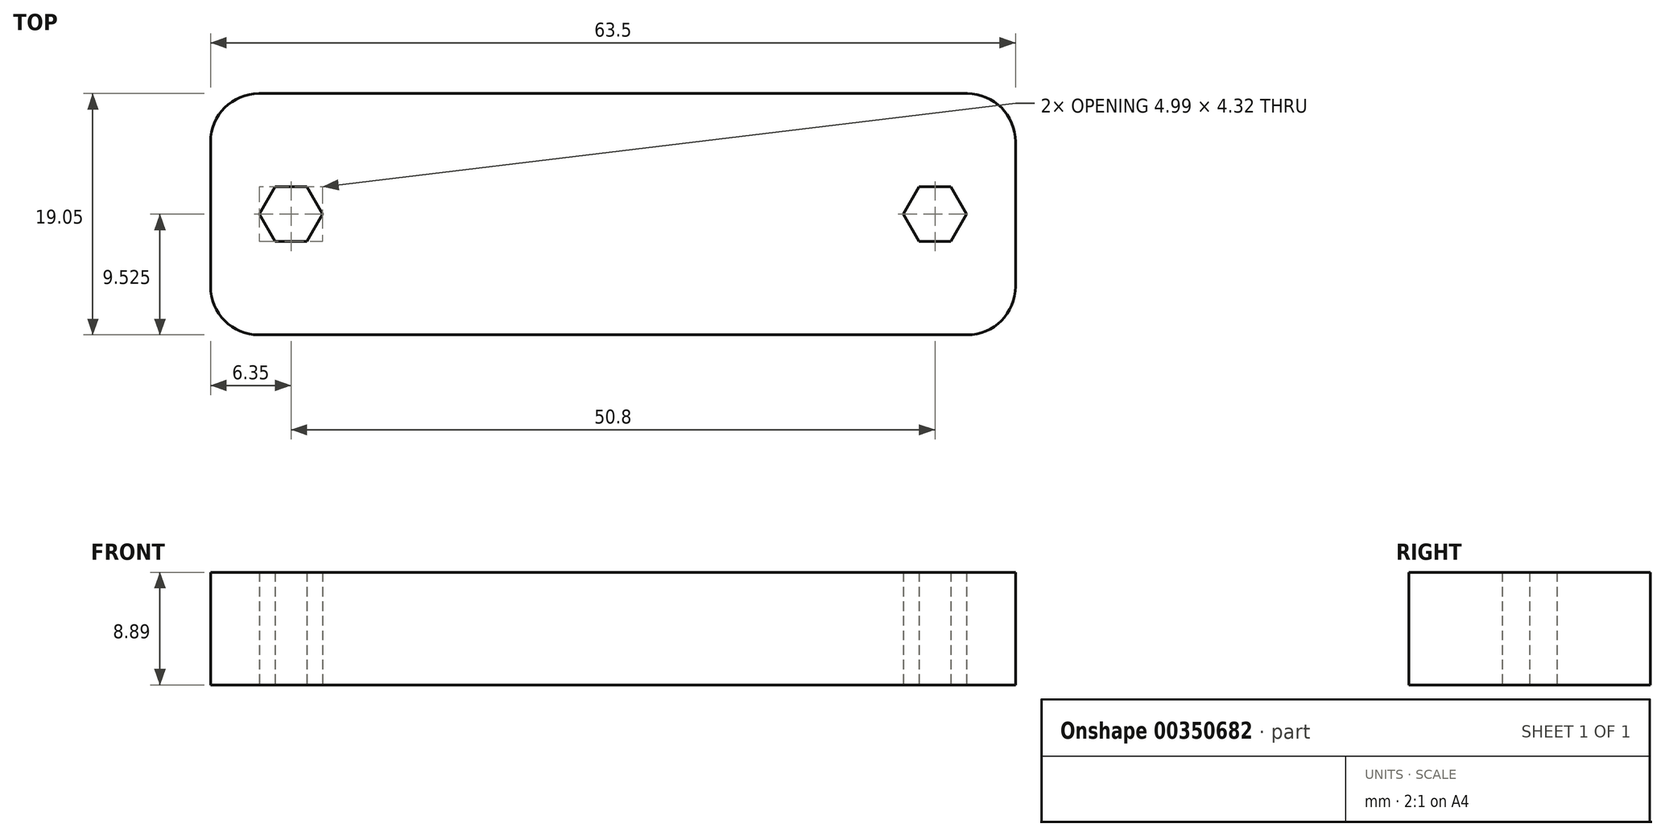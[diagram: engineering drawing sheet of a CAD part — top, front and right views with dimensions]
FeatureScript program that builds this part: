
annotation { "Feature Type Name" : "Feature", "Feature Type Description" : "" }
export const myFeature = defineFeature(function(context is Context, id is Id, definition is map)
    precondition{}
    {
        {
            var Q0;
            Q0=qCreatedBy(makeId("Top.planeOp"),FACE);
            var sketch = newSketch(context, id + "F0", { "sketchPlane" : qUnion([Q0])});
            skLineSegment(sketch, "E0.bottom", {"start": v(0, 0) * mm, "end": v(63.5, 0) * mm});
            skLineSegment(sketch, "E0.top", {"start": v(0, 19.05) * mm, "end": v(63.5, 19.05) * mm});
            skLineSegment(sketch, "E0.left", {"start": v(0, 0) * mm, "end": v(0, 19.05) * mm});
            skLineSegment(sketch, "E0.right", {"start": v(63.5, 0) * mm, "end": v(63.5, 19.05) * mm});
            skCircle(sketch, "E1.cCircle", {"center": v(6.35, 9.53) * mm, "radius": 2.16 * mm, "construction": true});
            skLineSegment(sketch, "E1.0", {"start": v(5.1, 11.68) * mm, "end": v(7.6, 11.68) * mm});
            skLineSegment(sketch, "E1.1", {"start": v(7.6, 11.68) * mm, "end": v(8.84, 9.53) * mm});
            skLineSegment(sketch, "E1.2", {"start": v(8.84, 9.52) * mm, "end": v(7.6, 7.37) * mm});
            skLineSegment(sketch, "E1.3", {"start": v(7.6, 7.37) * mm, "end": v(5.1, 7.37) * mm});
            skLineSegment(sketch, "E1.4", {"start": v(5.1, 7.37) * mm, "end": v(3.86, 9.53) * mm});
            skLineSegment(sketch, "E1.5", {"start": v(3.86, 9.53) * mm, "end": v(5.1, 11.68) * mm});
            skPoint(sketch, "E1.0.midPoint", {"position": v(6.35, 11.68) * mm});
            skCircle(sketch, "E2.cCircle", {"center": v(57.15, 9.53) * mm, "radius": 2.16 * mm, "construction": true});
            skLineSegment(sketch, "E2.0", {"start": v(55.9, 11.68) * mm, "end": v(58.4, 11.68) * mm});
            skLineSegment(sketch, "E2.1", {"start": v(58.4, 11.68) * mm, "end": v(59.64, 9.53) * mm});
            skLineSegment(sketch, "E2.2", {"start": v(59.64, 9.52) * mm, "end": v(58.4, 7.37) * mm});
            skLineSegment(sketch, "E2.3", {"start": v(58.4, 7.37) * mm, "end": v(55.9, 7.37) * mm});
            skLineSegment(sketch, "E2.4", {"start": v(55.9, 7.37) * mm, "end": v(54.66, 9.53) * mm});
            skLineSegment(sketch, "E2.5", {"start": v(54.66, 9.53) * mm, "end": v(55.9, 11.68) * mm});
            skPoint(sketch, "E2.0.midPoint", {"position": v(57.15, 11.68) * mm});
            skLineSegment(sketch, "E3", {"start": v(31.75, 19.05) * mm, "end": v(31.75, 0) * mm, "construction": true});
            skSolve(sketch);
        }
        {
            var Q0;
            Q0=makeQuery(id+"F0.imprint","IMPRINT",FACE,{"disambiguationData":[TD([[makeQuery(id+"F0.imprint","IMPRINT",EDGE,{"derivedFrom":sQuery(id+"F0.wireOp",EDGE,"E0.bottom")}),1.0]])]});
            extrude(context, id + "F1", {"entities" : qUnion([Q0]), "depth" : 8.9 * mm});
        }
        {
            var Q0;
            Q0=makeQuery(id+"F1.opExtrude","SWEPT_EDGE",EDGE,{"disambiguationData":[OSD([sQuery(id+"F0.wireOp",EDGE,"E0.bottom"),sQuery(id+"F0.wireOp",EDGE,"E0.left")])]});
            var Q1;
            Q1=makeQuery(id+"F1.opExtrude","SWEPT_EDGE",EDGE,{"disambiguationData":[OSD([sQuery(id+"F0.wireOp",EDGE,"E0.top"),sQuery(id+"F0.wireOp",EDGE,"E0.left")])]});
            var Q2;
            Q2=makeQuery(id+"F1.opExtrude","SWEPT_EDGE",EDGE,{"disambiguationData":[OSD([sQuery(id+"F0.wireOp",EDGE,"E0.bottom"),sQuery(id+"F0.wireOp",EDGE,"E0.right")])]});
            var Q3;
            Q3=makeQuery(id+"F1.opExtrude","SWEPT_EDGE",EDGE,{"disambiguationData":[OSD([sQuery(id+"F0.wireOp",EDGE,"E0.top"),sQuery(id+"F0.wireOp",EDGE,"E0.right")])]});
            fillet(context, id + "F2", {"entities" : qUnion([Q0, Q1, Q2, Q3]), "radius" : 3.8 * mm, "tangentPropagation" : true, "allowEdgeOverflow" : false});
        }
    });
